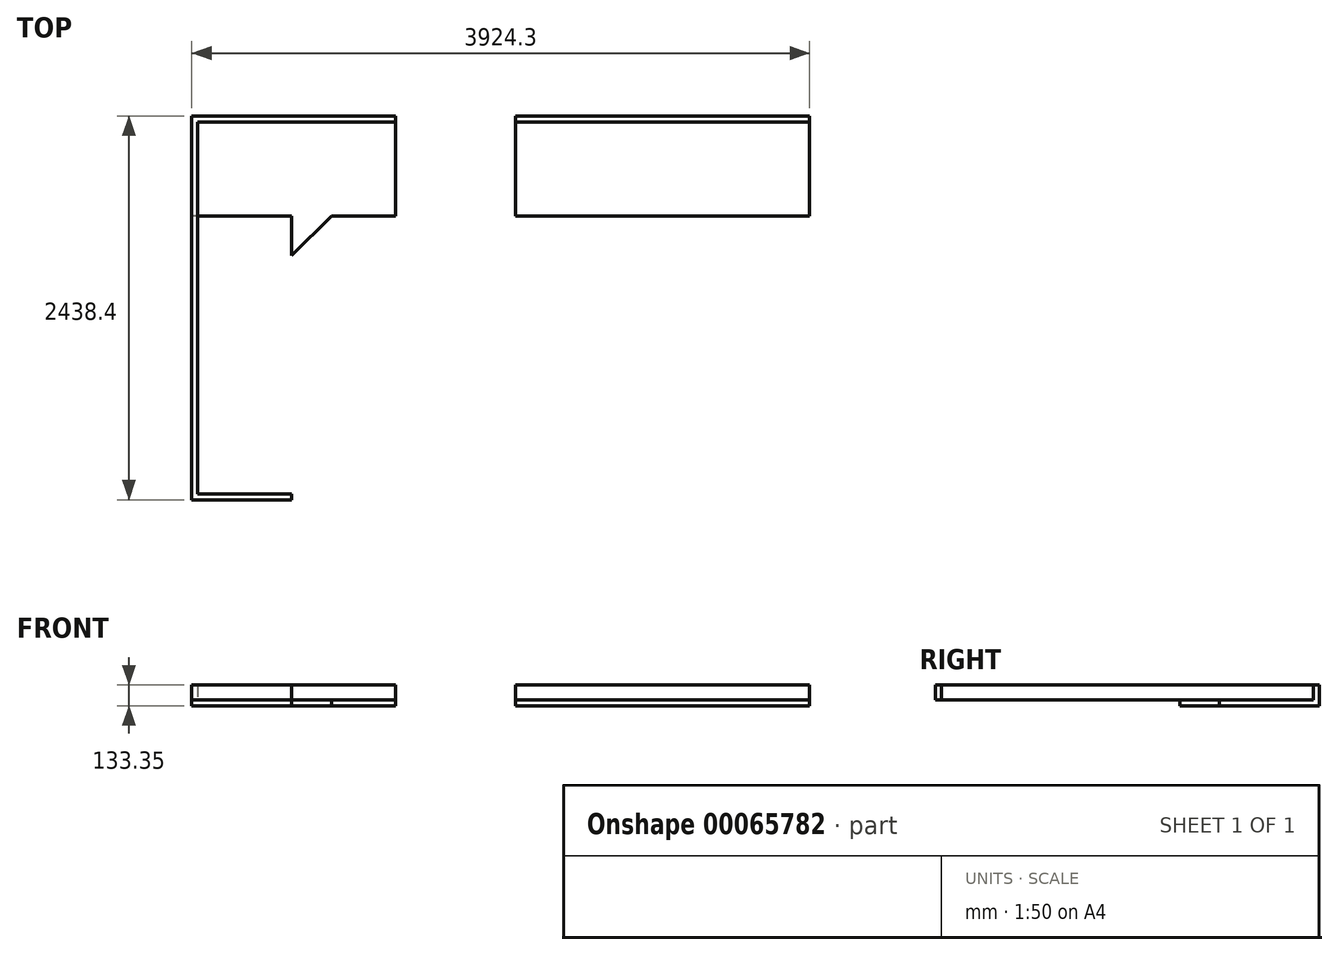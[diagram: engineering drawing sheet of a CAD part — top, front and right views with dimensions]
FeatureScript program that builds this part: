
annotation { "Feature Type Name" : "Feature", "Feature Type Description" : "" }
export const myFeature = defineFeature(function(context is Context, id is Id, definition is map)
    precondition{}
    {
        {
            var Q0;
            Q0=qCreatedBy(makeId("Top.planeOp"),FACE);
            var sketch = newSketch(context, id + "F0", { "sketchPlane" : qUnion([Q0])});
            skLineSegment(sketch, "E0.rect.bottom", {"start": v(1943.1, 317.5) * mm, "end": v(-1943.1, 317.5) * mm});
            skLineSegment(sketch, "E0.rect.top", {"start": v(1943.1, -317.5) * mm, "end": v(-1943.1, -317.5) * mm});
            skLineSegment(sketch, "E0.rect.left", {"start": v(1943.1, 317.5) * mm, "end": v(1943.1, -317.5) * mm});
            skLineSegment(sketch, "E0.rect.right", {"start": v(-1943.1, 317.5) * mm, "end": v(-1943.1, -317.5) * mm});
            skPoint(sketch, "E0.rect.middle", {"position": v(0, 0) * mm});
            skLineSegment(sketch, "E1.bottom", {"start": v(1943.1, 317.5) * mm, "end": v(1981.2, 317.5) * mm});
            skLineSegment(sketch, "E1.top", {"start": v(1943.1, -317.5) * mm, "end": v(1981.2, -317.5) * mm});
            skLineSegment(sketch, "E1.right", {"start": v(1981.2, 317.5) * mm, "end": v(1981.2, -317.5) * mm});
            skLineSegment(sketch, "E2.bottom", {"start": v(-1943.1, -317.5) * mm, "end": v(-1308.1, -317.5) * mm});
            skLineSegment(sketch, "E2.top", {"start": v(-1943.1, -2120.9) * mm, "end": v(-1308.1, -2120.9) * mm});
            skLineSegment(sketch, "E2.left", {"start": v(-1943.1, -317.5) * mm, "end": v(-1943.1, -2120.9) * mm});
            skLineSegment(sketch, "E2.right", {"start": v(-1308.1, -317.5) * mm, "end": v(-1308.1, -2120.9) * mm});
            skLineSegment(sketch, "E3", {"start": v(-1308.1, -568.95) * mm, "end": v(-1056.65, -317.5) * mm});
            skSolve(sketch);
        }
        {
            var Q0;
            Q0=makeQuery(id+"F0.imprint","IMPRINT",FACE,{"disambiguationData":[TD([[makeQuery(id+"F0.imprint","IMPRINT",EDGE,{"derivedFrom":sQuery(id+"F0.wireOp",EDGE,"E0.rect.bottom")}),1.0]])]});
            var Q1;
            Q1=makeQuery(id+"F0.imprint","IMPRINT",FACE,{"disambiguationData":[TD([[makeQuery(id+"F0.imprint","IMPRINT",EDGE,{"derivedFrom":sQuery(id+"F0.wireOp",EDGE,"E2.bottom")}),-1.0]])]});
            var Q2;
            Q2=makeQuery(id+"F0.imprint","IMPRINT",FACE,{"disambiguationData":[TD([[makeQuery(id+"F0.imprint","IMPRINT",EDGE,{"derivedFrom":sQuery(id+"F0.wireOp",EDGE,"E1.bottom")}),-1.0]])]});
            var Q3;
            {var subQ3=sQuery(id+"F0.wireOp",EDGE,"E3");Q3=makeQuery(id+"F0.imprint","IMPRINT",FACE,{"disambiguationData":[TD([[makeQuery(id+"F0.imprint","IMPRINT",EDGE,{"derivedFrom":subQ3}),1.0]])]});}
            extrude(context, id + "F1", {"entities" : qUnion([Q0, Q1, Q2, Q3]), "depth" : 38.1 * mm});
        }
        {
            var Q0;
            Q0=makeQuery(id+"F0.imprint","IMPRINT",FACE,{"disambiguationData":[TD([[makeQuery(id+"F0.imprint","IMPRINT",EDGE,{"derivedFrom":sQuery(id+"F0.wireOp",EDGE,"E1.bottom")}),-1.0]])]});
            extrude(context, id + "F2", {"entities" : qUnion([Q0]), "operationType" : NewBodyOperationType.ADD, "oppositeDirection" : true, "depth" : 876.3 * mm});
        }
        {
            var Q0;
            Q0=makeQuery(id+"F1.opExtrude","CAP_FACE",FACE,{"disambiguationData":[OSD([sQuery(id+"F0.wireOp",EDGE,"E0.rect.bottom"),sQuery(id+"F0.wireOp",EDGE,"E0.rect.top"),sQuery(id+"F0.wireOp",EDGE,"E0.rect.right"),sQuery(id+"F0.wireOp",EDGE,"E1.bottom"),sQuery(id+"F0.wireOp",EDGE,"E1.top"),sQuery(id+"F0.wireOp",EDGE,"E1.right"),sQuery(id+"F0.wireOp",EDGE,"E2.top"),sQuery(id+"F0.wireOp",EDGE,"E2.left"),sQuery(id+"F0.wireOp",EDGE,"E2.right")])],"isStart":false});
            var sketch = newSketch(context, id + "F3", { "sketchPlane" : qUnion([Q0])});
            skLineSegment(sketch, "E4.bottom", {"start": v(-1943.1, -2120.9) * mm, "end": v(-1905, -2120.9) * mm});
            skLineSegment(sketch, "E4.top", {"start": v(-1943.1, 317.5) * mm, "end": v(-1905, 317.5) * mm});
            skLineSegment(sketch, "E4.left", {"start": v(-1943.1, -2120.9) * mm, "end": v(-1943.1, 317.5) * mm});
            skLineSegment(sketch, "E4.right", {"start": v(-1905, -2082.8) * mm, "end": v(-1905, 279.4) * mm});
            skLineSegment(sketch, "E5.bottom", {"start": v(-1943.1, 317.5) * mm, "end": v(1981.2, 317.5) * mm});
            skLineSegment(sketch, "E5.top", {"start": v(-1905, 279.4) * mm, "end": v(1981.2, 279.4) * mm});
            skLineSegment(sketch, "E5.left", {"start": v(-1943.1, 317.5) * mm, "end": v(-1943.1, 279.4) * mm});
            skLineSegment(sketch, "E5.right", {"start": v(1981.2, 317.5) * mm, "end": v(1981.2, 279.4) * mm});
            skLineSegment(sketch, "E6.bottom", {"start": v(-1905, -2120.9) * mm, "end": v(-1308.1, -2120.9) * mm});
            skLineSegment(sketch, "E6.top", {"start": v(-1905, -2082.8) * mm, "end": v(-1308.1, -2082.8) * mm});
            skLineSegment(sketch, "E6.right", {"start": v(-1308.1, -2120.9) * mm, "end": v(-1308.1, -2082.8) * mm});
            skSolve(sketch);
        }
        {
            var Q0;
            Q0=qSketchRegion(id+"F3",true);
            extrude(context, id + "F4", {"entities" : qUnion([Q0]), "operationType" : NewBodyOperationType.ADD, "depth" : 95.25 * mm});
        }
        {
            var Q0;
            Q0=makeQuery(id+"F1.opExtrude","CAP_FACE",FACE,{"disambiguationData":[OSD([sQuery(id+"F0.wireOp",EDGE,"E0.rect.bottom"),sQuery(id+"F0.wireOp",EDGE,"E0.rect.top"),sQuery(id+"F0.wireOp",EDGE,"E0.rect.right"),sQuery(id+"F0.wireOp",EDGE,"E1.bottom"),sQuery(id+"F0.wireOp",EDGE,"E1.top"),sQuery(id+"F0.wireOp",EDGE,"E1.right"),sQuery(id+"F0.wireOp",EDGE,"E2.top"),sQuery(id+"F0.wireOp",EDGE,"E2.left"),sQuery(id+"F0.wireOp",EDGE,"E2.right"),sQuery(id+"F0.wireOp",EDGE,"E3")])],"isStart":false});
            var sketch = newSketch(context, id + "F5", { "sketchPlane" : qUnion([Q0])});
            skLineSegment(sketch, "E7.bottom", {"start": v(114.3, -317.5) * mm, "end": v(-647.7, -317.5) * mm});
            skLineSegment(sketch, "E7.top", {"start": v(114.3, 489.68) * mm, "end": v(-647.7, 489.68) * mm});
            skLineSegment(sketch, "E7.left", {"start": v(114.3, -317.5) * mm, "end": v(114.3, 489.68) * mm});
            skLineSegment(sketch, "E7.right", {"start": v(-647.7, -317.5) * mm, "end": v(-647.7, 489.68) * mm});
            skSolve(sketch);
        }
        {
            var Q0;
            Q0=qSketchRegion(id+"F5",true);
            extrude(context, id + "F6", {"entities" : qUnion([Q0]), "operationType" : NewBodyOperationType.REMOVE, "oppositeDirection" : true, "depth" : 203.2 * mm, "hasSecondDirection" : true, "secondDirectionOppositeDirection" : false, "secondDirectionDepth" : 203.2 * mm});
        }
        {
            var Q0;
            {var subQ0=sQuery(id+"F0.wireOp",EDGE,"E1.top");var subQ1=sQuery(id+"F0.wireOp",EDGE,"E2.right");var subQ2=sQuery(id+"F0.wireOp",EDGE,"E3");var subQ3=sQuery(id+"F0.wireOp",EDGE,"E0.rect.top");Q0=makeQuery(id+"F6.boolean.opBoolean","SPLIT",FACE,{"disambiguationData":[TD([makeQuery(id+"F1.opExtrude","SWEPT_FACE",FACE,{"disambiguationData":[OSD([subQ1])]})])],"derivedFrom":makeQuery(id+"F1.opExtrude","CAP_FACE",FACE,{"disambiguationData":[OSD([sQuery(id+"F0.wireOp",EDGE,"E0.rect.bottom"),subQ3,sQuery(id+"F0.wireOp",EDGE,"E0.rect.right"),sQuery(id+"F0.wireOp",EDGE,"E1.bottom"),subQ0,sQuery(id+"F0.wireOp",EDGE,"E1.right"),sQuery(id+"F0.wireOp",EDGE,"E2.top"),sQuery(id+"F0.wireOp",EDGE,"E2.left"),subQ1,subQ2])],"isStart":false})});}
            var sketch = newSketch(context, id + "F7", { "sketchPlane" : qUnion([Q0])});
            skLineSegment(sketch, "E8.rect.bottom", {"start": v(-1460.5, -647.7) * mm, "end": v(-1714.5, -647.7) * mm});
            skLineSegment(sketch, "E8.rect.top", {"start": v(-1460.5, -1460.5) * mm, "end": v(-1714.5, -1460.5) * mm});
            skLineSegment(sketch, "E8.rect.left", {"start": v(-1358.9, -749.3) * mm, "end": v(-1358.9, -1358.9) * mm});
            skLineSegment(sketch, "E8.rect.right", {"start": v(-1816.1, -749.3) * mm, "end": v(-1816.1, -1358.9) * mm});
            skPoint(sketch, "E8.rect.middle", {"position": v(-1587.5, -1054.1) * mm});
            skPoint(sketch, "E9.visualSharp", {"position": v(-1816.1, -1460.5) * mm});
            skArc(sketch, "E9.filletArc", {"start": v(-1816.1, -1358.9) * mm, "mid": v(-1786.34, -1430.74) * mm, "end": v(-1714.5, -1460.5) * mm});
            skPoint(sketch, "E10.visualSharp", {"position": v(-1358.9, -1460.5) * mm});
            skArc(sketch, "E10.filletArc", {"start": v(-1460.5, -1460.5) * mm, "mid": v(-1388.66, -1430.74) * mm, "end": v(-1358.9, -1358.9) * mm});
            skPoint(sketch, "E11.visualSharp", {"position": v(-1816.1, -647.7) * mm});
            skArc(sketch, "E11.filletArc", {"start": v(-1714.5, -647.7) * mm, "mid": v(-1786.34, -677.46) * mm, "end": v(-1816.1, -749.3) * mm});
            skPoint(sketch, "E12.visualSharp", {"position": v(-1358.9, -647.7) * mm});
            skArc(sketch, "E12.filletArc", {"start": v(-1358.9, -749.3) * mm, "mid": v(-1388.66, -677.46) * mm, "end": v(-1460.5, -647.7) * mm});
            skLineSegment(sketch, "E13", {"start": v(-1587.5, -1054.1) * mm, "end": v(-1854.2, -1054.1) * mm, "construction": true});
            skPoint(sketch, "E13.endSnap0", {"position": v(-1816.1, -1054.1) * mm});
            skCircle(sketch, "E14", {"center": v(-1854.2, -1054.1) * mm, "radius": 12.7 * mm});
            skSolve(sketch);
        }
        {
            var Q0;
            Q0=qSketchRegion(id+"F7",true);
            extrude(context, id + "F8", {"entities" : qUnion([Q0]), "operationType" : NewBodyOperationType.REMOVE, "oppositeDirection" : true, "depth" : 127 * mm});
        }
        {
            var Q0;
            Q0=makeQuery(id+"F2.opExtrude","SWEPT_FACE",FACE,{"disambiguationData":[OSD([sQuery(id+"F0.wireOp",EDGE,"E0.rect.left")])]});
            extrude(context, id + "F9", {"entities" : qUnion([Q0]), "operationType" : NewBodyOperationType.REMOVE, "oppositeDirection" : true, "depth" : 127 * mm});
        }
    });
